# Revit family: 2019_ES_Ventana_Qsystems_Q77+_1-Hoja
name_source: partatom
category: Windows
units: mm (PartAtom-declared; Revit-internal decimal feet)

## family parameters
Always vertical = Yes
Cut with Voids When Loaded = No
Host = Wall
OmniClass Number = 23.30.20.00
OmniClass Title = Windows
Room Calculation Point = No
Shared = No

## types (2) — shared parameters
Acabado = Anodizado, lacado y acabados
Acristalamiento = Cristal - Vidrio claro templado
Altura Real = 1000 mm  [stored 3.28084 ft]
Altura de antepecho por defecto = 800 mm  [stored 2.62467 ft]
Altura maxima = 2500 mm  [stored 8.2021 ft]
Altura minima = 600 mm  [stored 1.9685 ft]
Analytic Construction = <None>
AnchoPoliamidaHoja = 30 mm  [stored 0.0984252 ft]
AnchoPoliamidaMarco = 30 mm  [stored 0.0984252 ft]
Anchura Maxima = 1700 mm  [stored 5.57743 ft]
Anchura Minima = 100 mm  [stored 0.328084 ft]
Anchura Real = 600 mm  [stored 1.9685 ft]
Area = 600000 mm²
Autor = Bimetica Parametric Design Services, S.L.
BIMsupport = https://bimsupport.info
Bimetica = http://www.bimetica.com
COBieCategoria = IfcWindow
Catálogo (URL) = https://qsystemsaluminio.com
CerramientoExterior = Yes
Clasificacion acustica = 45 (-2,-6) dB
ConfiguracionPoliamidas = 273800 - 493700 - 493800
ControlHumos = No
CosteEnergeticoMj = 0 J
Desfase Acristalamiento = 13 mm
Detalle Perfileria = Yes
EstanqueidadAgua = E1650
FechaEmisionElementoBIM = 03/12/2021
FechaVencimientoElementoBIM = 03/12/2022
FraccionAreaAcristalamiento = 62.89%
GrosorAcristalamiento = 30 mm  [stored 0.0984252 ft]
GrosorMarco = 77 mm  [stored 0.252625 ft]
Gubimclass Codigo = 30.10.20.10
Gubimclass Titulo = Ventanas de fachadas
Height = 1000 mm  [stored 3.28084 ft]
Historial = (RVT2019) Actualziación a estándar GDO-BIM y datos.(RVT2015) Creación del Elemento.
IfcExportAs = IfcWindow
InformacionTecnica = http://www.alueuropa.com
Manija = Yes
Manufacturer = QSystems
Marcado CE = No
Marco = Aluminio Anodizado, lacado
MasterformatCodigo = 08 51 13
MasterformatTitulo = Aluminium Windows
Motorizada = No
Numero de Licencia = XXX-XXXX9536
OmniclassCodigo = 23.30.20.17.21.21
OmniclassTitulo = Casment Window
Perimetro = 3200
PermeabilidadAlAire = Clase 4
Peso = 0.00 kg
Plataforma descaga contenido BIM = www.bimetica.com
Poliamida = Technoform polyamide
Practicable = Yes
Proyección Apertura = Yes
PuntoDeContacto = QSystems
Referencia = Q77+
ReferenciaContacto = QSystems
RepisaExterior = Yes
RepisaInterior = Yes
ResistenciaAlViento = Clase C5
Rough Height = 605 mm
Rough Width = 1005 mm  [stored 3.29724 ft]
SalidaEmergencia = No
Serie = Q77+
TelefonoContacto = +34 91 895 58 00
Titular = Alueuropa S.A.
UNSPSCCodigo = 30171600
UNSPSCTitulo = Windows
URL = http://www.alueuropa.com
URL Perfil BIM = https://bimetica.com
URL Poliamida = http://www.technoform.es
URL Poliamida - Catálogo = http://www.technoform.com
URLProducto = https://qsystemsaluminio.com
Uniclass2.0Codigo = 25-30
Uniclass2.0Titulo = Door and window systems
Version = RVT2019
Version Estandar GDO-BIM = GDO-BIM V02
Wall Closure = By host
Width = 600 mm  [stored 1.9685 ft]
Y𝑔 = 0.11
𝐴𝑓 = 245616
𝐴𝑔 = 354384
𝑈𝑓 = 3.629
𝑈𝑔 = 1.9
𝑈𝑤 = 3.068317
𝑙𝑔 = 2512
zero-valued in all types: AcidificacionAtmosferica, AcidificacionAtmosfericaPorUnidad, AguaConsumida, AguaConsumidaPorUnidad, CambioClimatico, CambioClimaticoPorUnidad, CosteEnergeticoKwh, CosteMantenimiento, DestruccionCapaOzonoEstratosferica, DestruccionCapaOzonoEstratosfericaPorUnidad, EmisionCO2, Energia consumida, EnergiaNoRenovableConsumida, EnergiaNoRenovableConsumidaPorUnidad, EnergiaPrimariaTotalConsumida, EnergiaPrimariaTotalConsumidaPorUnidad, EnergiaRenovableConsumida, EnergiaRenovableConsumidaPorUnidad, Eutrofizacion, EutrofizacionPorUnidad, FactorSolarModificado, FactorSombra, FaltaDeRecursos, FaltaDeRecursosPorUnidad, FormacionFotoquimicaOzono, FormacionFotoquimicaOzonoPorUnidad, Fraccion de area de acristalamiento, GrosorMaximoAcristalamiento, GrosorMinimoAcristalamiento, Infiltracion, Profundidad, ResiduoInerte, ResiduoInertePorUnidad, ResiduoRadioactivo, ResiduoRadioactivoPorUnidad, ResiduosNoPeligrosos, ResiduosNoPeligrososPorUnidad, ResiduosPeligrosos, ResiduosPeligrososPorUnidad, Transmitancia termica, TransmitanciaTermica

## per-type parameters (varying)
| type | Description | IfcExportType | Model | Operation | Oscilobatiente | Type Comments |
| 600x1000 mm Practicable | Ventana 1 Hoja Practicable | Ventana Practicable | Q77 Practicable | Practicable | No | Sistema de Ventana con Rotura de Puente Térmico Q77 Practicable. |
| 600x1000 mm Oscilobatiente | Ventana 1 Hoja Oscilobatiente | Ventana Oscilobatiente | Q77 Oscilobatiente | Oscilobatiente | Yes | Sistema de Ventana con Rotura de Puente Térmico Q77 Oscilobatiente. |

note: [stored X ft] marks values corroborated as IEEE doubles in the binary element streams (Revit-internal decimal feet)

## geometry (parser evidence)
native form markers: Blend x2
no freeform markers — native parametric forms only
